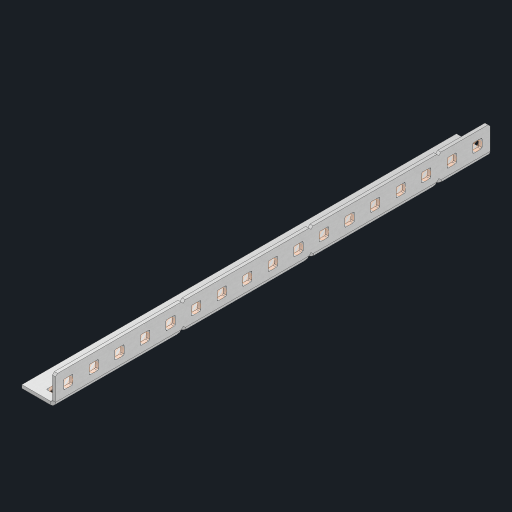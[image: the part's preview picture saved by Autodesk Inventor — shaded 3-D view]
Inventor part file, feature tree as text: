
AUTODESK INVENTOR PART (.ipt)
format: ipt  version: 2023 (Build 270158000, 158)  size: 718,848 bytes
history: native  units: in
note: dims shown in document units (in); Inventor stores cm internally (conversion verified against a paired STEP export)
features: other x39, extrude x33, sheet_metal_op x10, sketch x8, mirror x1, pattern_linear x1, chamfer x1
ambient origin geometry x8: Origin, YZ Plane, XZ Plane, XY Plane, X Axis, Y Axis, Z Axis, Center Point
bodies: Solid1 (feature_tree), Body (feature_tree)
feature tree (93):
  other  "Flange Pattern Plane"
  sheet_metal_op  "Flange Pattern"
  sheet_metal_op  "Body Pattern"
  other  "Arc Length"
  mirror  "Notch Mirror"
  pattern_linear  "Notch Pattern"  Spacing1=0.25in  [1 undecoded]
  chamfer  "End Chamfer"
  extrude  "Half Cut"  Depth=0.0625in
  sketch  "Sketch1"  dims[d0=1.5in]
  other  "Plate1"
  sketch  "Sketch2"  dims[d1=8.5in]
  other  "Plate2"
  sheet_metal_op  "Bend1"
  sheet_metal_op  "Corner1"
  sketch  "Sketch3"  dims[d2=0.0625in]
  other  "Flange Pattern Sketch"
  sketch  "Sketch7"  dims[d3=0.0625in]
  other  "Srf1"
  other  "Srf2"
  sketch  "Sketch8"  dims[d4=0.0312in]
  sketch  "Sketch9"  dims[d5=0.125in]
  other  "Srf91"
  sheet_metal_op  "Body Pattern Sketch"
  other  "Srf92"
  sketch  "Sketch13"  dims[d6=0.0625in]
  sketch  "Sketch14"  dims[d7=0.5in d8=90.0deg d9=0.0312in d10=0.25in d11=0.0625in d12=0.0625in d16=0.182in d17=0.02in d18=0.0625in d19=0.0in d20=0.25in d21=0.25in d46=0.172in d47=1.0in d48=0.0in d49=0.182in d50=0.02in d51=0.25in d52=0.25in d53=0.0625in d54=0.0in d55=0.172in d56=1.0in d57=0.0in d60=6.6929in d62=0.5in d63=0.3937in d65=0.5in d85=0.1473in d86=0.1782in d88=0.04in d89=0.0625in d90=0.0in d91=0.04in d92=0.0491in d95=2.5in d96=0.04in d97=0.25in d98=45.0deg d101=0.0in d102=2.497in d131=0.5in d132=6.6929in d134=0.5in d139=0.5in]
  other  "Srf856"
  other  "Srf1310"
  other  "Srf1311"
  other  "Srf1312"
  other  "Srf1376"
  other  "Srf1377"
  other  "Srf1728"
  other  "Srf1755"
  other  "Srf1878"
  other  "Srf1879"
  other  "Srf1880"
  other  "Srf1881"
  other  "Srf1882"
  other  "Srf1883"
  other  "Srf1884"
  other  "Srf1885"
  other  "Srf1886"
  other  "Srf1887"
  other  "Srf1888"
  other  "Srf1942"
  other  "Srf1943"
  other  "Srf1944"
  other  "Srf1945"
  other  "Srf1946"
  other  "Srf1947"
  other  "Srf1948"
  other  "Srf1949"
  other  "Srf1950"
  other  "Srf1951"
  other  "Srf1952"
  sheet_metal_op  "Flange Stamp"
  sheet_metal_op  "Flange Circle"
  sheet_metal_op  "Body Stamp"
  sheet_metal_op  "Body Circle"
  sheet_metal_op  "Notch"
  extrude  "ExtrusionSrf2"  Depth=0.0625in
  extrude  "ExtrusionSrf92"  Depth=0.5in
  extrude  "ExtrusionSrf856"  Depth=0.02in
  extrude  "ExtrusionSrf1310"  Depth=0.0625in
  extrude  "ExtrusionSrf1311"  TaperAngle=0.0deg  [1 undecoded]
  extrude  "ExtrusionSrf1312"  Depth=0.5in
  extrude  "ExtrusionSrf1376"  Depth=0.5in
  extrude  "ExtrusionSrf1377"  Depth=0.5in
  extrude  "ExtrusionSrf1728"  Depth=0.5in TaperAngle=0.0deg
  extrude  "ExtrusionSrf1755"  Depth=0.5in
  extrude  "ExtrusionSrf1878"  Depth=0.02in
  extrude  "ExtrusionSrf1879"  Depth=0.5in
  extrude  "ExtrusionSrf1880"  Depth=0.5in
  extrude  "ExtrusionSrf1881"  Depth=0.0625in
  extrude  "ExtrusionSrf1882"  TaperAngle=0.0deg  [1 undecoded]
  extrude  "ExtrusionSrf1883"  Depth=0.5in
  extrude  "ExtrusionSrf1884"  Depth=0.5in TaperAngle=0.0deg
  extrude  "ExtrusionSrf1885"  Depth=0.5in
  extrude  "ExtrusionSrf1886"  Depth=0.5in
  extrude  "ExtrusionSrf1887"  Depth=0.5in
  extrude  "ExtrusionSrf1888"  Depth=0.5in
  extrude  "ExtrusionSrf1942"  Depth=0.5in
  extrude  "ExtrusionSrf1943"  Depth=0.0625in
  extrude  "ExtrusionSrf1944"  TaperAngle=0.0deg  [1 undecoded]
  extrude  "ExtrusionSrf1945"  Depth=0.5in
  extrude  "ExtrusionSrf1946"  Depth=0.5in
  extrude  "ExtrusionSrf1947"  Depth=0.5in
  extrude  "ExtrusionSrf1948"  Depth=0.5in TaperAngle=45.0deg
  extrude  "ExtrusionSrf1949"  TaperAngle=0.0deg  [1 undecoded]
  extrude  "ExtrusionSrf1950"  Depth=0.5in
  extrude  "ExtrusionSrf1951"  Depth=0.5in
  extrude  "ExtrusionSrf1952"  Depth=0.5in
note: 5 required parameter values undecoded (feature->parameter linkage not recoverable at this tier; creation-order binding heuristic only, values carry confidence <= 0.55)
